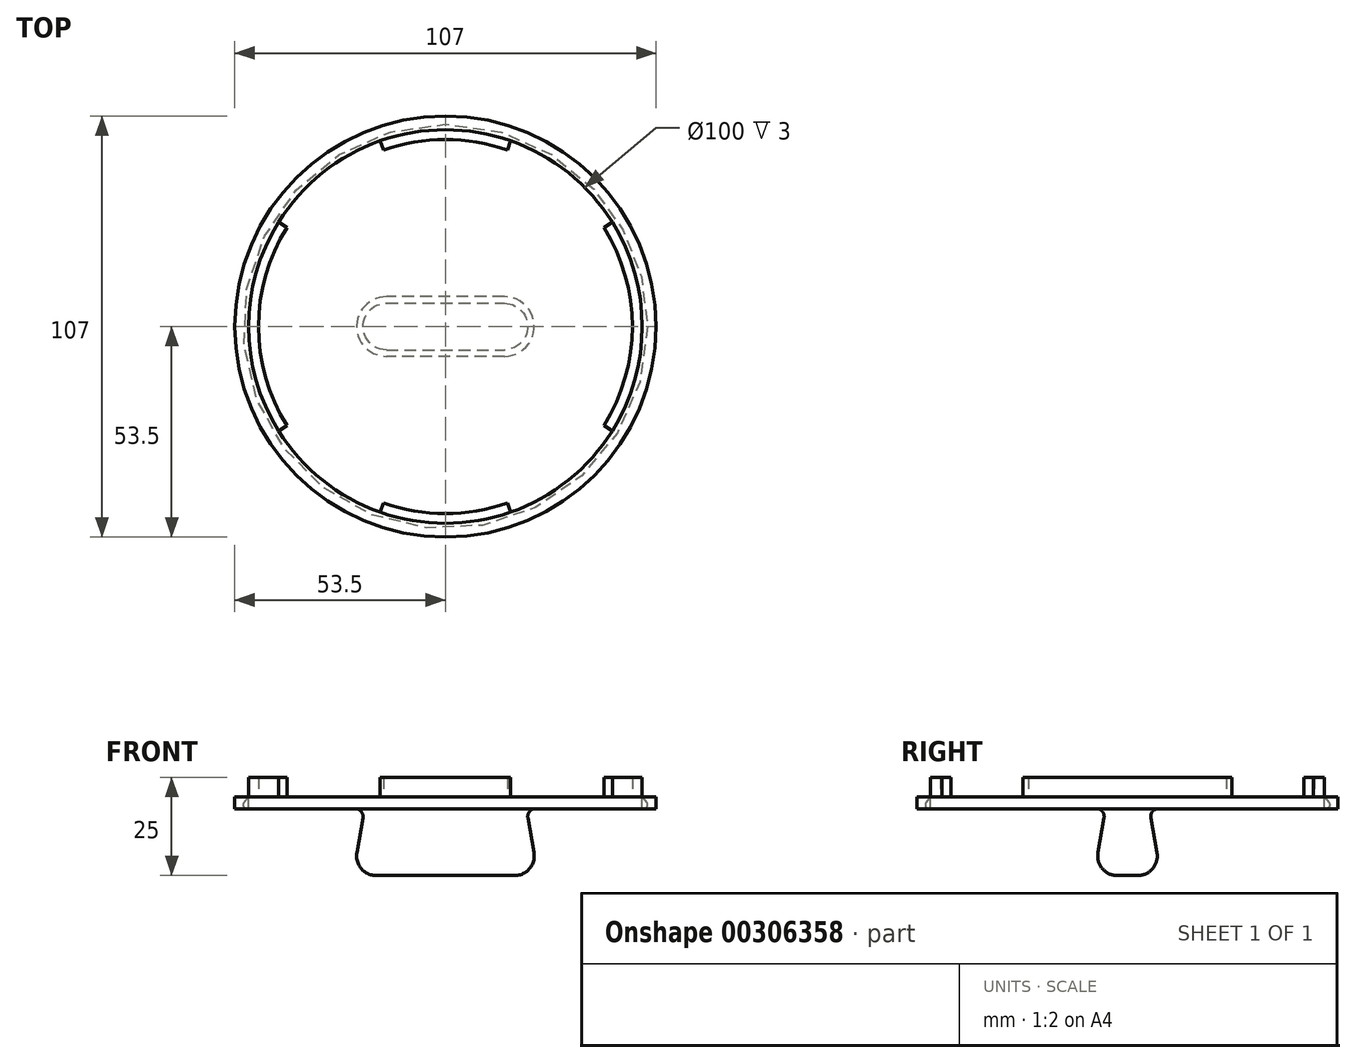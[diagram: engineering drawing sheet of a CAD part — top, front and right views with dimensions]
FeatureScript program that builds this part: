
annotation { "Feature Type Name" : "Feature", "Feature Type Description" : "" }
export const myFeature = defineFeature(function(context is Context, id is Id, definition is map)
    precondition{}
    {
        {
            var Q0;
            Q0=qCreatedBy(makeId("Top.planeOp"),FACE);
            var sketch = newSketch(context, id + "F0", { "sketchPlane" : qUnion([Q0])});
            skCircle(sketch, "E0", {"center": v(0, 0) * mm, "radius": 53.5 * mm});
            skCircle(sketch, "E1", {"center": v(0, 0) * mm, "radius": 50 * mm});
            skCircle(sketch, "E2", {"center": v(0, 0) * mm, "radius": 47.5 * mm});
            skLineSegment(sketch, "E3", {"start": v(-15.72, 44.82) * mm, "end": v(-16.55, 47.18) * mm});
            skLineSegment(sketch, "E4.MirrorCS", {"start": v(15.72, 44.82) * mm, "end": v(16.55, 47.18) * mm});
            skLineSegment(sketch, "E5.MirrorCS", {"start": v(-15.72, -44.82) * mm, "end": v(-16.55, -47.18) * mm});
            skLineSegment(sketch, "E6.MirrorCS", {"start": v(15.72, -44.82) * mm, "end": v(16.55, -47.18) * mm});
            skLineSegment(sketch, "E7.MirrorCS", {"start": v(-40.27, 25.18) * mm, "end": v(-42.4, 26.5) * mm});
            skLineSegment(sketch, "E8.MirrorCS", {"start": v(40.27, 25.18) * mm, "end": v(42.4, 26.5) * mm});
            skLineSegment(sketch, "E9.MirrorCS", {"start": v(-40.27, -25.18) * mm, "end": v(-42.4, -26.5) * mm});
            skLineSegment(sketch, "E10.MirrorCS", {"start": v(40.27, -25.18) * mm, "end": v(42.4, -26.5) * mm});
            skPoint(sketch, "E11.start.orphan", {"position": v(0, 66.31) * mm});
            skPoint(sketch, "E12.start.orphan", {"position": v(-68.54, 0) * mm});
            skSolve(sketch);
        }
        {
            var Q0;
            Q0=makeQuery(id+"F0.imprint","IMPRINT",FACE,{"disambiguationData":[TD([[makeQuery(id+"F0.imprint","IMPRINT",EDGE,{"derivedFrom":sQuery(id+"F0.wireOp",EDGE,"E0")}),1.0]])]});
            var Q1;
            Q1=sQuery(id+"F0.wireOp",EDGE,"E0");
            extrude(context, id + "F1", {"entities" : qUnion([Q0]), "surfaceEntities" : qUnion([Q1]), "oppositeDirection" : true, "depth" : 3 * mm});
        }
        {
            var Q0;
            {var subQ0=sQuery(id+"F0.wireOp",EDGE,"E3");Q0=makeQuery(id+"F0.imprint","IMPRINT",FACE,{"disambiguationData":[TD([[makeQuery(id+"F0.imprint","IMPRINT",EDGE,{"derivedFrom":subQ0}),-1.0]])]});}
            var Q1;
            {var subQ0=sQuery(id+"F0.wireOp",EDGE,"E8.MirrorCS");Q1=makeQuery(id+"F0.imprint","IMPRINT",FACE,{"disambiguationData":[TD([[makeQuery(id+"F0.imprint","IMPRINT",EDGE,{"derivedFrom":subQ0}),-1.0]])]});}
            var Q2;
            {var subQ0=sQuery(id+"F0.wireOp",EDGE,"E7.MirrorCS");Q2=makeQuery(id+"F0.imprint","IMPRINT",FACE,{"disambiguationData":[TD([[makeQuery(id+"F0.imprint","IMPRINT",EDGE,{"derivedFrom":subQ0}),1.0]])]});}
            var Q3;
            {var subQ0=sQuery(id+"F0.wireOp",EDGE,"E5.MirrorCS");Q3=makeQuery(id+"F0.imprint","IMPRINT",FACE,{"disambiguationData":[TD([[makeQuery(id+"F0.imprint","IMPRINT",EDGE,{"derivedFrom":subQ0}),1.0]])]});}
            extrude(context, id + "F2", {"entities" : qUnion([Q0, Q1, Q2, Q3]), "depth" : 5 * mm});
        }
        {
            var Q0;
            Q0=qCreatedBy(makeId("Top.planeOp"),FACE);
            var sketch = newSketch(context, id + "F3", { "sketchPlane" : qUnion([Q0])});
            skCircle(sketch, "E13", {"center": v(0, 0) * mm, "radius": 50 * mm});
            skLineSegment(sketch, "E14.bottom", {"start": v(-15, -5) * mm, "end": v(15, -5) * mm});
            skLineSegment(sketch, "E14.top", {"start": v(-15, 5) * mm, "end": v(15, 5) * mm});
            skLineSegment(sketch, "E14.left", {"start": v(-20, 0) * mm, "end": v(-20, 0) * mm});
            skLineSegment(sketch, "E14.right", {"start": v(20, 0) * mm, "end": v(20, 0) * mm});
            skPoint(sketch, "E15.visualSharp", {"position": v(-20, -5) * mm});
            skArc(sketch, "E15.filletArc", {"start": v(-20, 0) * mm, "mid": v(-18.54, -3.54) * mm, "end": v(-15, -5) * mm});
            skPoint(sketch, "E16.visualSharp", {"position": v(-20, 5) * mm});
            skArc(sketch, "E16.filletArc", {"start": v(-15, 5) * mm, "mid": v(-18.54, 3.54) * mm, "end": v(-20, 0) * mm});
            skPoint(sketch, "E17.visualSharp", {"position": v(20, 5) * mm});
            skArc(sketch, "E17.filletArc", {"start": v(20, 0) * mm, "mid": v(18.54, 3.54) * mm, "end": v(15, 5) * mm});
            skPoint(sketch, "E18.visualSharp", {"position": v(20, -5) * mm});
            skArc(sketch, "E18.filletArc", {"start": v(15, -5) * mm, "mid": v(18.54, -3.54) * mm, "end": v(20, 0) * mm});
            skSolve(sketch);
        }
        {
            var Q0;
            Q0=makeQuery(id+"F3.imprint","IMPRINT",FACE,{"disambiguationData":[TD([[makeQuery(id+"F3.imprint","IMPRINT",EDGE,{"derivedFrom":sQuery(id+"F3.wireOp",EDGE,"E13")}),1.0]])]});
            extrude(context, id + "F4", {"entities" : qUnion([Q0]), "oppositeDirection" : true, "depth" : 3 * mm, "hasDraft" : true, "draftAngle" : 40 * degree});
        }
        {
            var Q0;
            Q0=makeQuery(id+"F3.imprint","IMPRINT",FACE,{"disambiguationData":[TD([[makeQuery(id+"F3.imprint","IMPRINT",EDGE,{"derivedFrom":sQuery(id+"F3.wireOp",EDGE,"E14.bottom")}),1.0]])]});
            extrude(context, id + "F5", {"entities" : qUnion([Q0]), "operationType" : NewBodyOperationType.ADD, "oppositeDirection" : true, "depth" : 20 * mm, "hasDraft" : true, "draftAngle" : 10 * degree});
        }
        {
            var Q0;
            {var subQ0=sQuery(id+"F3.wireOp",EDGE,"E14.top");Q0=makeQuery(id+"F5.boolean.opBoolean","INTERSECT",EDGE,{"derivedFrom":[makeQuery(id+"F4.opExtrude","CAP_FACE",FACE,{"disambiguationData":[OSD([sQuery(id+"F3.wireOp",EDGE,"E13"),sQuery(id+"F3.wireOp",EDGE,"E14.bottom"),subQ0,sQuery(id+"F3.wireOp",EDGE,"E15.filletArc"),sQuery(id+"F3.wireOp",EDGE,"E16.filletArc"),sQuery(id+"F3.wireOp",EDGE,"E17.filletArc"),sQuery(id+"F3.wireOp",EDGE,"E18.filletArc")])],"isStart":false}),makeQuery(id+"F5.opExtrude","SWEPT_FACE",FACE,{"disambiguationData":[OSD([subQ0])]})]});}
            fillet(context, id + "F6", {"entities" : qUnion([Q0]), "radius" : 2 * mm, "tangentPropagation" : true, "allowEdgeOverflow" : false});
        }
        {
            var Q0;
            Q0=makeQuery(id+"F5.opExtrude","CAP_FACE",FACE,{"disambiguationData":[OSD([sQuery(id+"F3.wireOp",EDGE,"E14.bottom"),sQuery(id+"F3.wireOp",EDGE,"E14.top"),sQuery(id+"F3.wireOp",EDGE,"E15.filletArc"),sQuery(id+"F3.wireOp",EDGE,"E16.filletArc"),sQuery(id+"F3.wireOp",EDGE,"E17.filletArc"),sQuery(id+"F3.wireOp",EDGE,"E18.filletArc")])],"isStart":false});
            fillet(context, id + "F7", {"entities" : qUnion([Q0]), "radius" : 5 * mm, "tangentPropagation" : true, "allowEdgeOverflow" : false});
        }
        {
            var Q0;
            Q0=makeQuery(id+"F4.opExtrude","CAP_EDGE",EDGE,{"disambiguationData":[OSD([sQuery(id+"F3.wireOp",EDGE,"E13")])],"isStart":false});
            fillet(context, id + "F8", {"entities" : qUnion([Q0]), "radius" : 1 * mm, "tangentPropagation" : true, "allowEdgeOverflow" : false});
        }
    });
